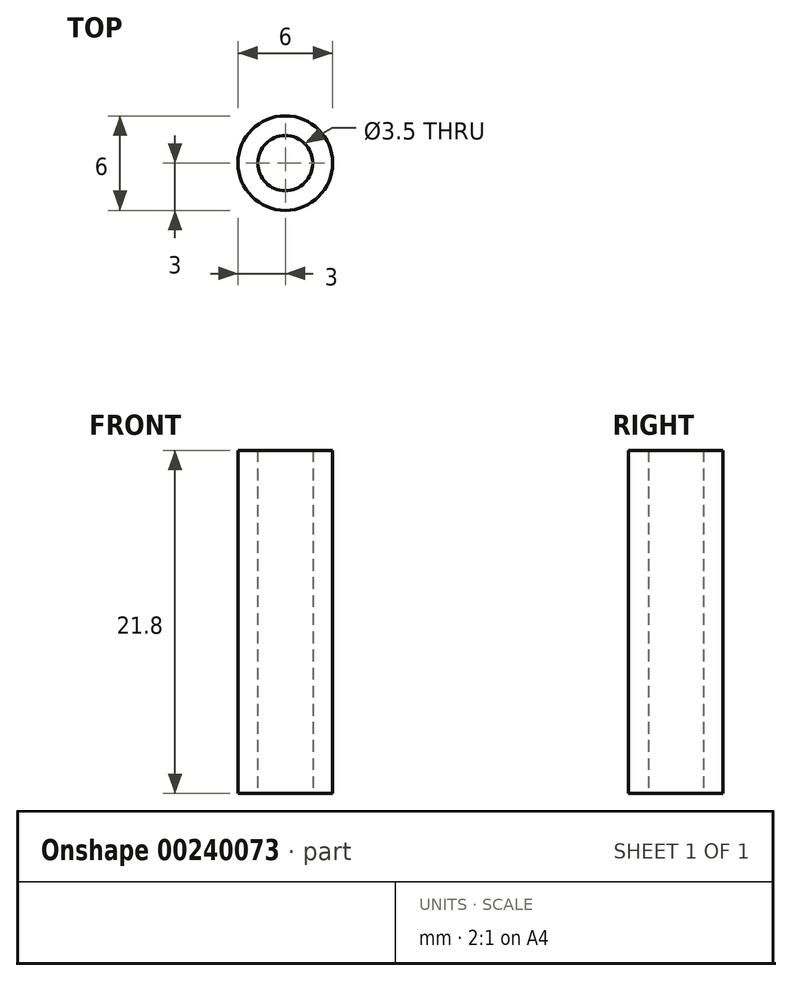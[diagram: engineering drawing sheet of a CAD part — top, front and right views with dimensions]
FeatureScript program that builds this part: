
annotation { "Feature Type Name" : "Feature", "Feature Type Description" : "" }
export const myFeature = defineFeature(function(context is Context, id is Id, definition is map)
    precondition{}
    {
        {
            var Q0;
            Q0=qCreatedBy(makeId("Top.planeOp"),FACE);
            var sketch = newSketch(context, id + "F0", { "sketchPlane" : qUnion([Q0])});
            skCircle(sketch, "E0", {"center": v(0, 0) * mm, "radius": 3 * mm});
            skSolve(sketch);
        }
        {
            var Q0;
            Q0=qSketchRegion(id+"F0",true);
            extrude(context, id + "F1", {"entities" : qUnion([Q0]), "depth" : 21.8 * mm});
        }
        {
            var Q0;
            Q0=sQuery(id+"F0.wireOp",VERTEX,"E0.center");
            var Q1;
            Q1=makeQuery(id+"F1.opExtrude","SWEPT_BODY",BODY,{"disambiguationData":[OSD([sQuery(id+"F0.wireOp",EDGE,"E0")])]});
            hole(context, id + "F2", {"style" : HoleStyle.SIMPLE, "endStyle" : HoleEndStyle.THROUGH, "oppositeDirection" : true, "holeDiameter" : 3.5 * mm, "locations" : qUnion([Q0]), "scope" : qUnion([Q1]), "tappedDepth" : 12 * mm, "tapClearance" : 3});
        }
    });
